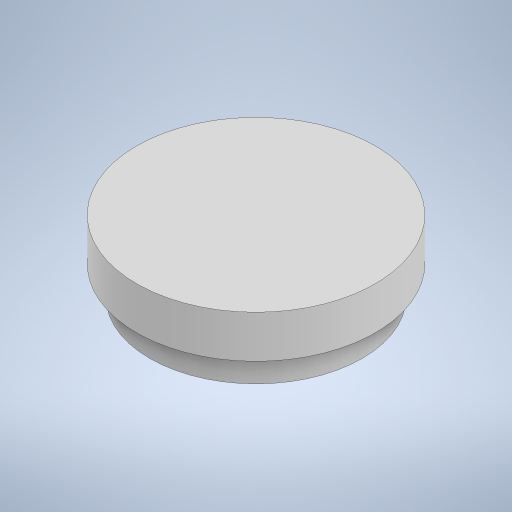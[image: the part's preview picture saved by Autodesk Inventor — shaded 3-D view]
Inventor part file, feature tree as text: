
AUTODESK INVENTOR PART (.ipt)
format: ipt  version: 2023 (Build 270158000, 158)  size: 211,968 bytes
history: native  units: in
note: dims shown in document units (in); Inventor stores cm internally (conversion verified against a paired STEP export)
features: extrude x2, sketch x1
ambient origin geometry x8: Origin, YZ Plane, XZ Plane, XY Plane, X Axis, Y Axis, Z Axis, Center Point
bodies: Solid1 (feature_tree)
feature tree (3):
  sketch  "Sketch1"  dims[d0=0.25in d1=0.281in d2=0.05in d3=0.0in d4=0.034in d5=0.0in]
  extrude  "Extrusion1"  Depth=0.034in
  extrude  "Extrusion2"  Depth=0.05in TaperAngle=0.0deg
